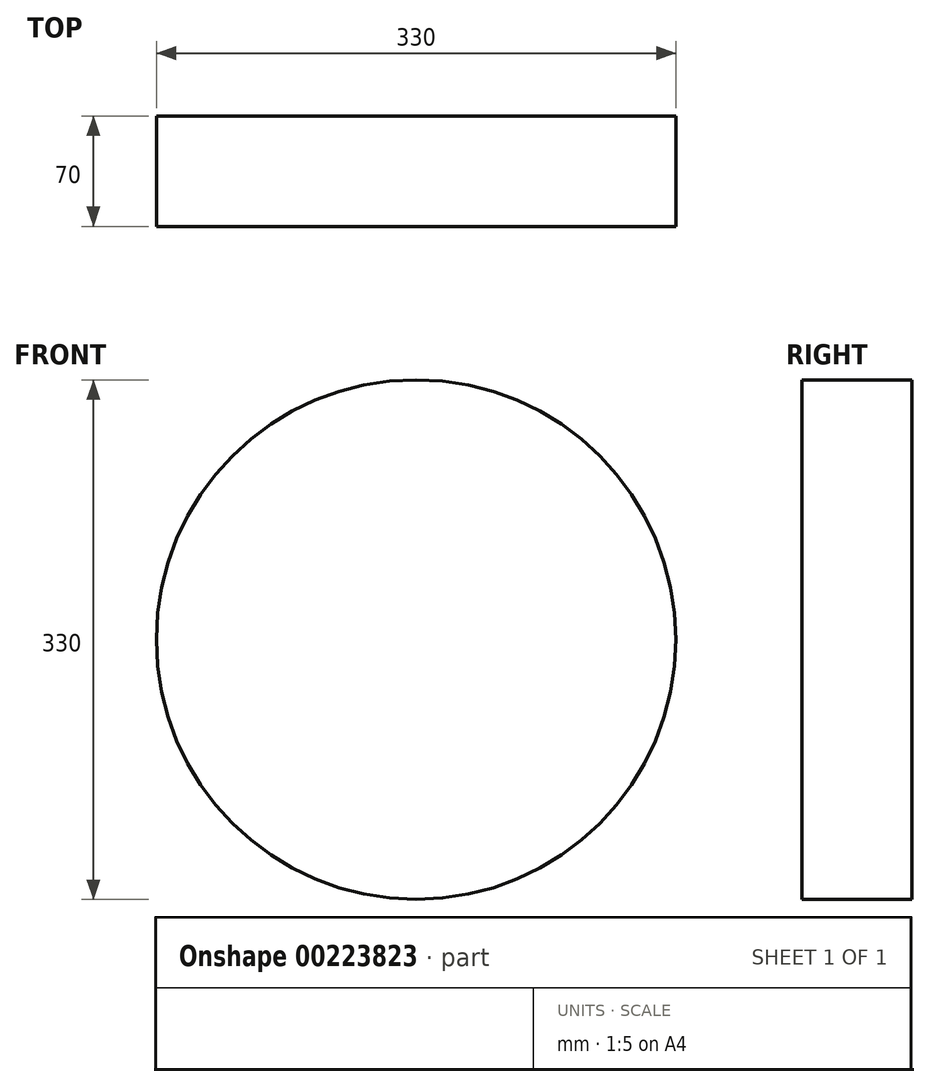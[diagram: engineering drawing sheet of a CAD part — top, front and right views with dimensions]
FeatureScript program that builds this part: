
annotation { "Feature Type Name" : "Feature", "Feature Type Description" : "" }
export const myFeature = defineFeature(function(context is Context, id is Id, definition is map)
    precondition{}
    {
        {
            var Q0;
            Q0=qCreatedBy(makeId("Front.planeOp"),FACE);
            var sketch = newSketch(context, id + "F0", { "sketchPlane" : qUnion([Q0])});
            skCircle(sketch, "E0", {"center": v(0, 0) * mm, "radius": 165 * mm});
            skSolve(sketch);
        }
        {
            var Q0;
            Q0 = qSketchRegion(id + "F0", true);
            extrude(context, id + "F1", {"entities" : qUnion([Q0]), "endBound" : BoundingType.SYMMETRIC, "depth" : 70 * mm});
        }
    });
